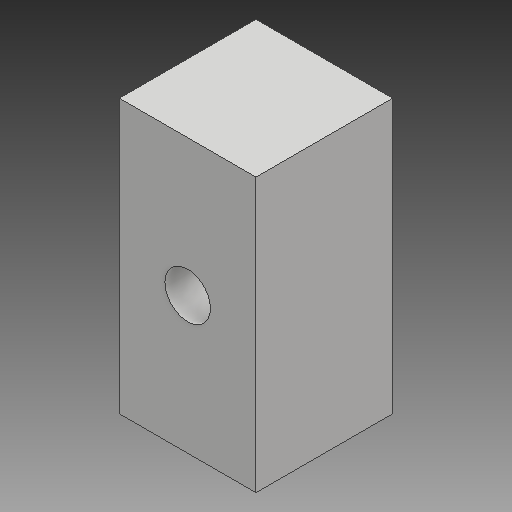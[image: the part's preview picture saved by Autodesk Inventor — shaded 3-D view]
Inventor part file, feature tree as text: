
AUTODESK INVENTOR PART (.ipt)
format: ipt  version: 2018 (Build 220112000, 112)  size: 87,040 bytes
history: native  units: mm
features: other x3, sketch x1
ambient origin geometry x8: Origin, YZ Plane, XZ Plane, XY Plane, X Axis, Y Axis, Z Axis, Center Point
bodies: Volumenkörper1 (feature_tree)
feature tree (4):
  other  "zweites Teil rotorachse.ipt"
  other  "Volumenkörper1::zweites Teil rotorachse.ipt"
  other  "Bezeichnung1"
  sketch  "Skizze1"  dims[d0=10.0mm]
